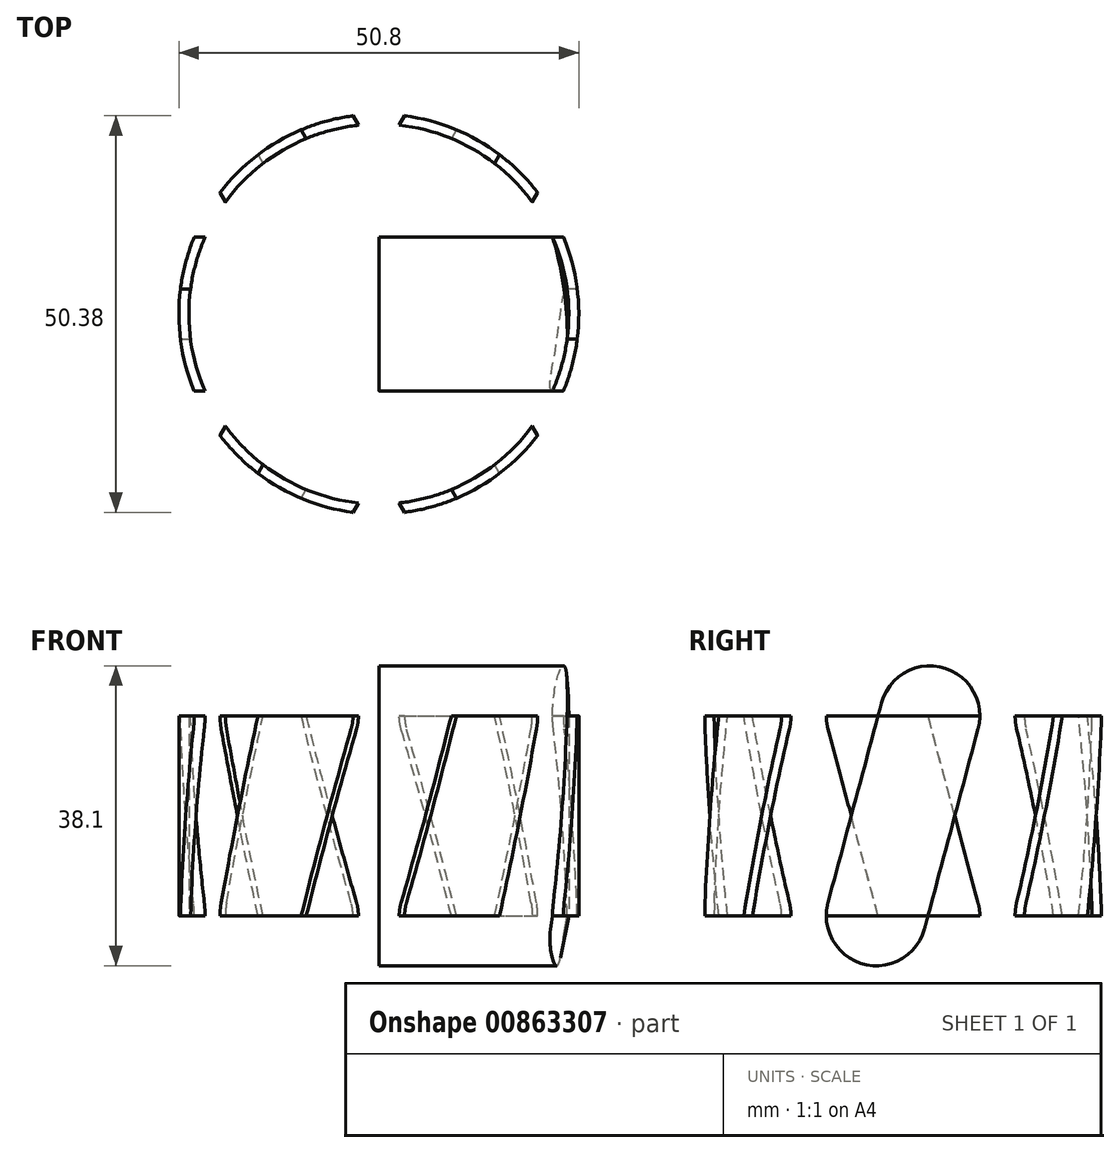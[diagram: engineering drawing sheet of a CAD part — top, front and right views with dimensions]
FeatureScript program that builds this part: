
annotation { "Feature Type Name" : "Feature", "Feature Type Description" : "" }
export const myFeature = defineFeature(function(context is Context, id is Id, definition is map)
    precondition{}
    {
        {
            var Q0;
            Q0=qCreatedBy(makeId("Right.planeOp"),FACE);
            var sketch = newSketch(context, id + "F0", { "sketchPlane" : qUnion([Q0])});
            skLineSegment(sketch, "E0", {"start": v(-16.8, 0) * mm, "end": v(-19.05, 0) * mm});
            skLineSegment(sketch, "E1", {"start": v(0, 6.35) * mm, "end": v(0, 25.4) * mm});
            skLineSegment(sketch, "E2", {"start": v(0, 25.4) * mm, "end": v(-24.13, 25.4) * mm});
            skLineSegment(sketch, "E3", {"start": v(-24.13, 25.4) * mm, "end": v(-19.05, 0) * mm});
            skLineSegment(sketch, "E4", {"start": v(-24.13, 25.4) * mm, "end": v(-24.13, 50.8) * mm});
            skLineSegment(sketch, "E5", {"start": v(0, 25.4) * mm, "end": v(0, 50.8) * mm});
            skLineSegment(sketch, "E6", {"start": v(0, 50.8) * mm, "end": v(25.4, 50.8) * mm});
            skArc(sketch, "E7", {"start": v(-3.06, 91.33) * mm, "mid": v(-18.55, 73.64) * mm, "end": v(-24.13, 50.8) * mm});
            skLineSegment(sketch, "E8", {"start": v(0, 50.8) * mm, "end": v(0, 93.32) * mm});
            skArc(sketch, "E9", {"start": v(0, 92.3) * mm, "mid": v(-1.6, 92.05) * mm, "end": v(-3.06, 91.33) * mm});
            skLineSegment(sketch, "E10", {"start": v(0, 0) * mm, "end": v(0, -19.05) * mm});
            skArc(sketch, "E11", {"start": v(0, 6.35) * mm, "mid": v(-8.98, 4.7) * mm, "end": v(-16.8, 0) * mm});
            skSolve(sketch);
        }
        {
            var Q0;
            Q0=makeQuery(id+"F0.imprint","IMPRINT",FACE,{"disambiguationData":[TD([[makeQuery(id+"F0.imprint","IMPRINT",EDGE,{"derivedFrom":sQuery(id+"F0.wireOp",EDGE,"E0")}),-1.0]])]});
            var Q1;
            Q1=makeQuery(id+"F0.imprint","IMPRINT",FACE,{"disambiguationData":[TD([[makeQuery(id+"F0.imprint","IMPRINT",EDGE,{"derivedFrom":sQuery(id+"F0.wireOp",EDGE,"E2")}),-1.0]])]});
            var Q2;
            Q2=sQuery(id+"F0.wireOp",EDGE,"E8");
            revolve(context, id + "F1", {"surfaceOperationType" : NewSurfaceOperationType.NEW, "entities" : qUnion([Q0, Q1]), "axis" : qUnion([Q2]), "revolveType" : RevolveType.FULL});
        }
        {
            var Q0;
            Q0=qCreatedBy(makeId("Right.planeOp"),FACE);
            var sketch = newSketch(context, id + "F2", { "sketchPlane" : qUnion([Q0])});
            skLineSegment(sketch, "E12", {"start": v(0, 0) * mm, "end": v(0, 25.4) * mm});
            skLineSegment(sketch, "E13", {"start": v(0, 25.4) * mm, "end": v(-25.4, 25.4) * mm});
            skLineSegment(sketch, "E14", {"start": v(-25.4, 25.4) * mm, "end": v(-25.4, 50.8) * mm});
            skLineSegment(sketch, "E15", {"start": v(-25.4, 50.8) * mm, "end": v(-24.13, 50.8) * mm});
            skLineSegment(sketch, "E16", {"start": v(-24.13, 50.8) * mm, "end": v(-24.13, 25.4) * mm});
            skSolve(sketch);
        }
        {
            var Q0;
            {var subQ0=sQuery(id+"F2.wireOp",EDGE,"E14");Q0=makeQuery(id+"F2.imprint","IMPRINT",FACE,{"disambiguationData":[TD([[makeQuery(id+"F2.imprint","IMPRINT",EDGE,{"derivedFrom":subQ0}),-1.0]])]});}
            var Q1;
            Q1=sQuery(id+"F2.wireOp",EDGE,"E12");
            revolve(context, id + "F3", {"surfaceOperationType" : NewSurfaceOperationType.NEW, "entities" : qUnion([Q0]), "axis" : qUnion([Q1]), "revolveType" : RevolveType.FULL});
        }
        {
            var Q0;
            Q0=qCreatedBy(makeId("Right.planeOp"),FACE);
            var sketch = newSketch(context, id + "F4", { "sketchPlane" : qUnion([Q0])});
            skLineSegment(sketch, "E17", {"start": v(0, 38.1) * mm, "end": v(-3.4, 25.4) * mm});
            skLineSegment(sketch, "E18", {"start": v(-3.4, 25.4) * mm, "end": v(3.4, 50.8) * mm});
            skPoint(sketch, "E19.orphan", {"position": v(0, 52.8) * mm});
            skPoint(sketch, "E20.orphan", {"position": v(0, 23.4) * mm});
            skPoint(sketch, "E21.orphan", {"position": v(-25.4, 52.8) * mm});
            skArc(sketch, "E22.0.startCap", {"start": v(2.73, 23.76) * mm, "mid": v(-5.05, 19.27) * mm, "end": v(-9.54, 27.04) * mm});
            skArc(sketch, "E22.0.endCap", {"start": v(-2.73, 52.44) * mm, "mid": v(5.05, 56.93) * mm, "end": v(9.54, 49.16) * mm});
            skLineSegment(sketch, "E22.0.left", {"start": v(-9.54, 27.04) * mm, "end": v(-2.73, 52.44) * mm});
            skLineSegment(sketch, "E22.0.right", {"start": v(2.73, 23.76) * mm, "end": v(9.54, 49.16) * mm});
            skSolve(sketch);
        }
        {
            var Q0;
            Q0 = qSketchRegion(id + "F4", true);
            extrude(context, id + "F5", {"entities" : qUnion([Q0]), "operationType" : NewBodyOperationType.INTERSECT, "depth" : 25.4 * mm, "offsetDistance" : 25.4 * mm});
        }
        {
            var Q0;
            Q0=makeQuery(id+"F3.opRevolve","SWEPT_BODY",BODY,{"disambiguationData":[OSD([sQuery(id+"F2.wireOp",EDGE,"E13"),sQuery(id+"F2.wireOp",EDGE,"E14"),sQuery(id+"F2.wireOp",EDGE,"E15"),sQuery(id+"F2.wireOp",EDGE,"E16")])]});
            var Q1;
            Q1=makeQuery(id+"F1.opRevolve","SWEPT_FACE",FACE,{"disambiguationData":[OSD([sQuery(id+"F0.wireOp",EDGE,"E4")])]});
            circularPattern(context, id + "F6", {"entities" : qUnion([Q0]), "axis" : qUnion([Q1]), "angle" : 360 * degree, "instanceCount" : 6, "equalSpace" : true});
        }
    });
